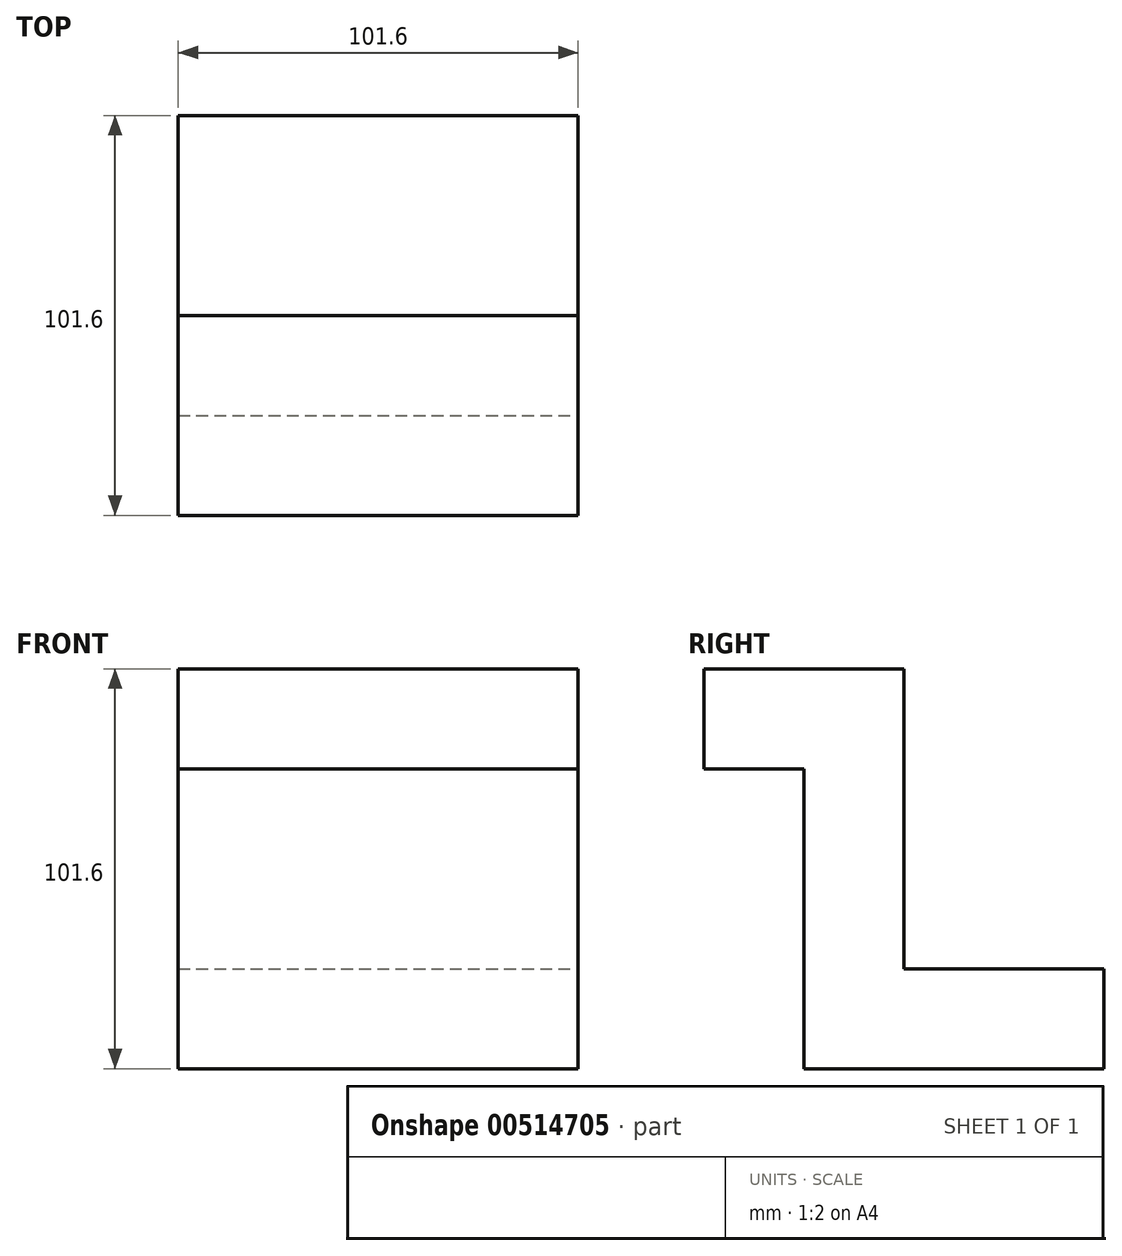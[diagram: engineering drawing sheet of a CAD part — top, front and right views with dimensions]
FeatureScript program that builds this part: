
annotation { "Feature Type Name" : "Feature", "Feature Type Description" : "" }
export const myFeature = defineFeature(function(context is Context, id is Id, definition is map)
    precondition{}
    {
        {
            var Q0;
            Q0=qCreatedBy(makeId("Top.planeOp"),FACE);
            var sketch = newSketch(context, id + "F0", { "sketchPlane" : qUnion([Q0])});
            skLineSegment(sketch, "E0.bottom", {"start": v(0, 0) * mm, "end": v(-101.6, 0) * mm});
            skLineSegment(sketch, "E0.top", {"start": v(0, -101.6) * mm, "end": v(-101.6, -101.6) * mm});
            skLineSegment(sketch, "E0.left", {"start": v(0, 0) * mm, "end": v(0, -101.6) * mm});
            skLineSegment(sketch, "E0.right", {"start": v(-101.6, 0) * mm, "end": v(-101.6, -101.6) * mm});
            skSolve(sketch);
        }
        {
            var Q0;
            Q0=makeQuery(id+"F0.imprint","IMPRINT",FACE,{"disambiguationData":[TD([[makeQuery(id+"F0.imprint","IMPRINT",EDGE,{"derivedFrom":sQuery(id+"F0.wireOp",EDGE,"E0.bottom")}),1.0]])]});
            extrude(context, id + "F1", {"entities" : qUnion([Q0]), "depth" : 101.6 * mm, "offsetDistance" : 25.4 * mm});
        }
        {
            var Q0;
            Q0=makeQuery(id+"F1.opExtrude","SWEPT_FACE",FACE,{"disambiguationData":[OSD([sQuery(id+"F0.wireOp",EDGE,"E0.left")])]});
            var sketch = newSketch(context, id + "F2", { "sketchPlane" : qUnion([Q0])});
            skLineSegment(sketch, "E1.bottom", {"start": v(-101.6, 0) * mm, "end": v(-76.2, 0) * mm});
            skLineSegment(sketch, "E1.top", {"start": v(-101.6, 76.2) * mm, "end": v(-76.2, 76.2) * mm});
            skLineSegment(sketch, "E1.left", {"start": v(-101.6, 0) * mm, "end": v(-101.6, 76.2) * mm});
            skLineSegment(sketch, "E1.right", {"start": v(-76.2, 0) * mm, "end": v(-76.2, 76.2) * mm});
            skLineSegment(sketch, "E2.bottom", {"start": v(0, 101.6) * mm, "end": v(-50.8, 101.6) * mm});
            skLineSegment(sketch, "E2.top", {"start": v(0, 25.4) * mm, "end": v(-50.8, 25.4) * mm});
            skLineSegment(sketch, "E2.left", {"start": v(0, 101.6) * mm, "end": v(0, 25.4) * mm});
            skLineSegment(sketch, "E2.right", {"start": v(-50.8, 101.6) * mm, "end": v(-50.8, 25.4) * mm});
            skSolve(sketch);
        }
        {
            var Q0;
            Q0=makeQuery(id+"F2.imprint","IMPRINT",FACE,{"disambiguationData":[TD([[makeQuery(id+"F2.imprint","IMPRINT",EDGE,{"derivedFrom":sQuery(id+"F2.wireOp",EDGE,"E1.bottom")}),-1.0]])]});
            var Q1;
            Q1=makeQuery(id+"F2.imprint","IMPRINT",FACE,{"disambiguationData":[TD([[makeQuery(id+"F2.imprint","IMPRINT",EDGE,{"derivedFrom":sQuery(id+"F2.wireOp",EDGE,"E2.bottom")}),1.0]])]});
            extrude(context, id + "F3", {"entities" : qUnion([Q0, Q1]), "operationType" : NewBodyOperationType.REMOVE, "oppositeDirection" : true, "depth" : 121.92 * mm, "offsetDistance" : 25.4 * mm});
        }
    });
